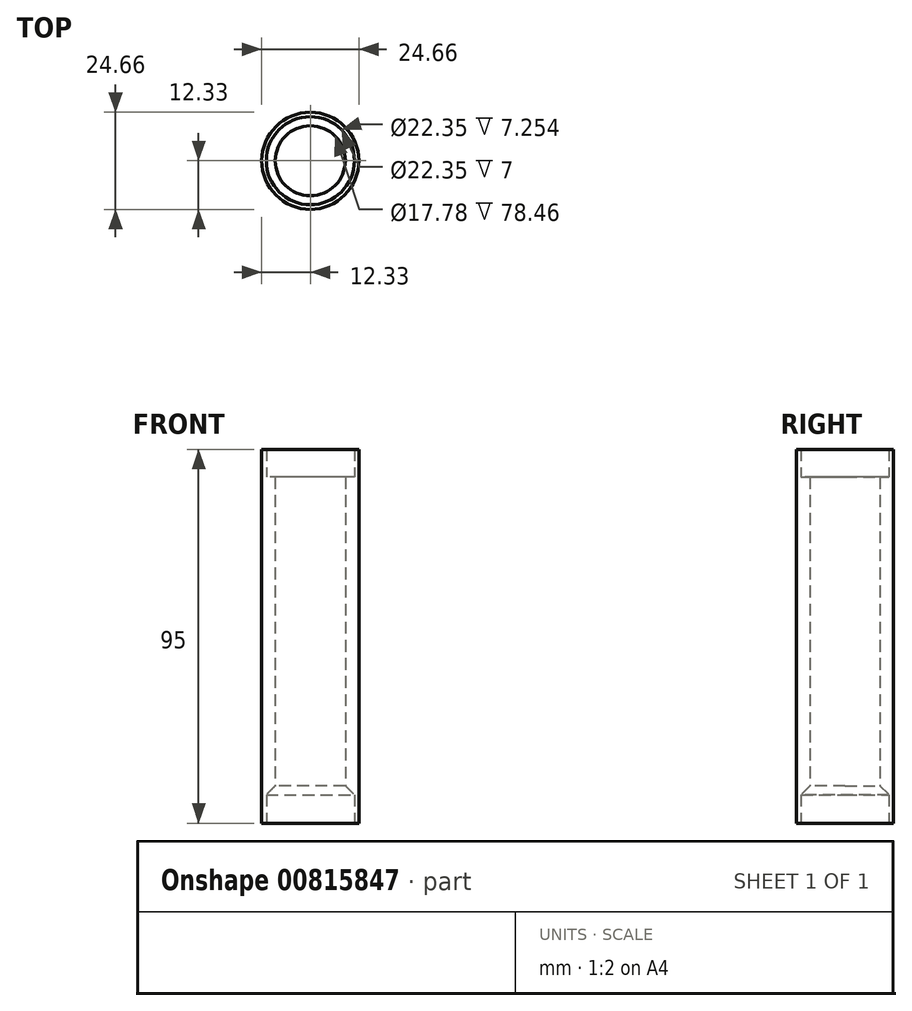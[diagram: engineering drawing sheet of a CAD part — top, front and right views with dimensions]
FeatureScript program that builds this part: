
annotation { "Feature Type Name" : "Feature", "Feature Type Description" : "" }
export const myFeature = defineFeature(function(context is Context, id is Id, definition is map)
    precondition{}
    {
        {
            var Q0;
            Q0=qCreatedBy(makeId("Top.planeOp"),FACE);
            var sketch = newSketch(context, id + "F0", { "sketchPlane" : qUnion([Q0])});
            skCircle(sketch, "E0", {"center": v(0, 0) * mm, "radius": 8.9 * mm});
            skCircle(sketch, "E1", {"center": v(0, 0) * mm, "radius": 11.18 * mm});
            skCircle(sketch, "E2", {"center": v(0, 0) * mm, "radius": 12.33 * mm});
            skSolve(sketch);
        }
        {
            var Q0;
            Q0=makeQuery(id+"F0.imprint","IMPRINT",FACE,{"disambiguationData":[TD([[makeQuery(id+"F0.imprint","IMPRINT",EDGE,{"derivedFrom":sQuery(id+"F0.wireOp",EDGE,"E1")}),-1.0]])]});
            extrude(context, id + "F1", {"entities" : qUnion([Q0]), "endBound" : BoundingType.SYMMETRIC, "depth" : 95 * mm, "offsetDistance" : 25.4 * mm});
        }
        {
            var Q0;
            Q0=makeQuery(id+"F0.imprint","IMPRINT",FACE,{"disambiguationData":[TD([[makeQuery(id+"F0.imprint","IMPRINT",EDGE,{"derivedFrom":sQuery(id+"F0.wireOp",EDGE,"E0")}),-1.0]])]});
            extrude(context, id + "F2", {"entities" : qUnion([Q0]), "operationType" : NewBodyOperationType.ADD, "endBound" : BoundingType.SYMMETRIC, "depth" : 81 * mm, "offsetDistance" : 25.4 * mm});
        }
        {
            var Q0;
            Q0=makeQuery(id+"F2.opExtrude","CAP_EDGE",EDGE,{"disambiguationData":[OSD([sQuery(id+"F0.wireOp",EDGE,"E0")])],"isStart":true});
            chamfer(context, id + "F3", {"entities" : qUnion([Q0]), "width" : 2.54 * mm, "tangentPropagation" : true});
        }
    });
